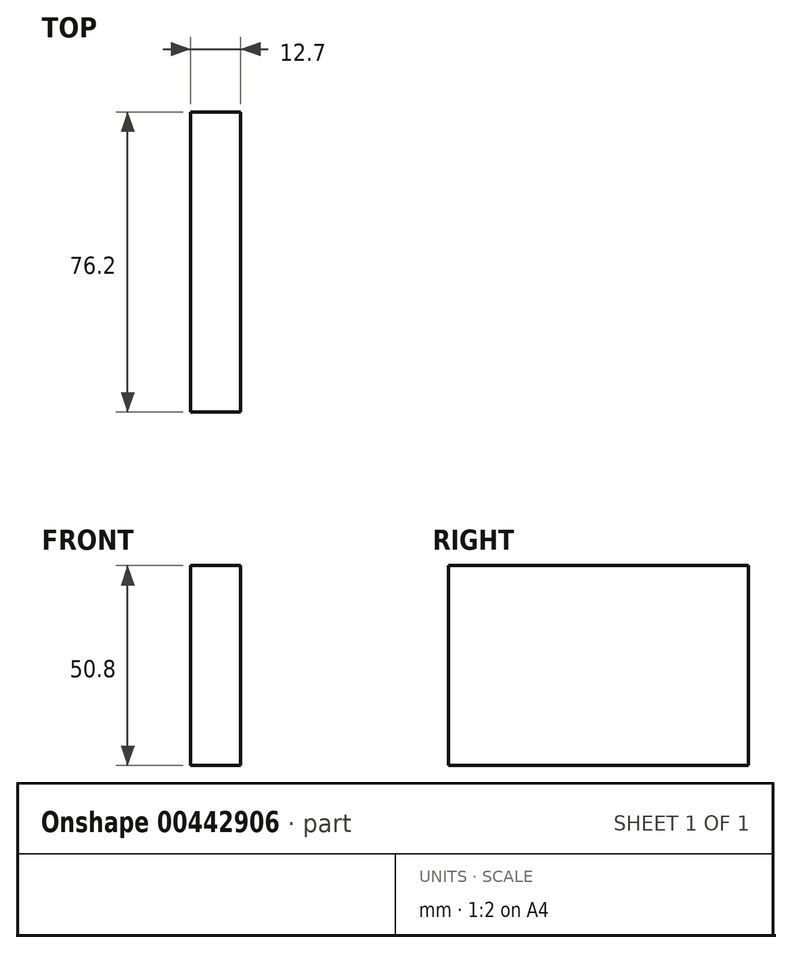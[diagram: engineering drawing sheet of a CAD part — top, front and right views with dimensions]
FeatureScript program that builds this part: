
annotation { "Feature Type Name" : "Feature", "Feature Type Description" : "" }
export const myFeature = defineFeature(function(context is Context, id is Id, definition is map)
    precondition{}
    {
        {
            var Q0;
            Q0=qCreatedBy(makeId("Right.planeOp"),FACE);
            var sketch = newSketch(context, id + "F0", { "sketchPlane" : qUnion([Q0])});
            skLineSegment(sketch, "E0.bottom", {"start": v(38.1, 25.4) * mm, "end": v(-38.1, 25.4) * mm});
            skLineSegment(sketch, "E0.top", {"start": v(38.1, -25.4) * mm, "end": v(-38.1, -25.4) * mm});
            skLineSegment(sketch, "E0.left", {"start": v(38.1, 25.4) * mm, "end": v(38.1, -25.4) * mm});
            skLineSegment(sketch, "E0.right", {"start": v(-38.1, 25.4) * mm, "end": v(-38.1, -25.4) * mm});
            skPoint(sketch, "E0.middle", {"position": v(0, 0) * mm});
            skSolve(sketch);
        }
        {
            var Q0;
            Q0=makeQuery(id+"F0.imprint","IMPRINT",FACE,{"disambiguationData":[TD([[makeQuery(id+"F0.imprint","IMPRINT",EDGE,{"derivedFrom":sQuery(id+"F0.wireOp",EDGE,"E0.bottom")}),1.0]])]});
            extrude(context, id + "F1", {"entities" : qUnion([Q0]), "depth" : 12.7 * mm});
        }
    });
